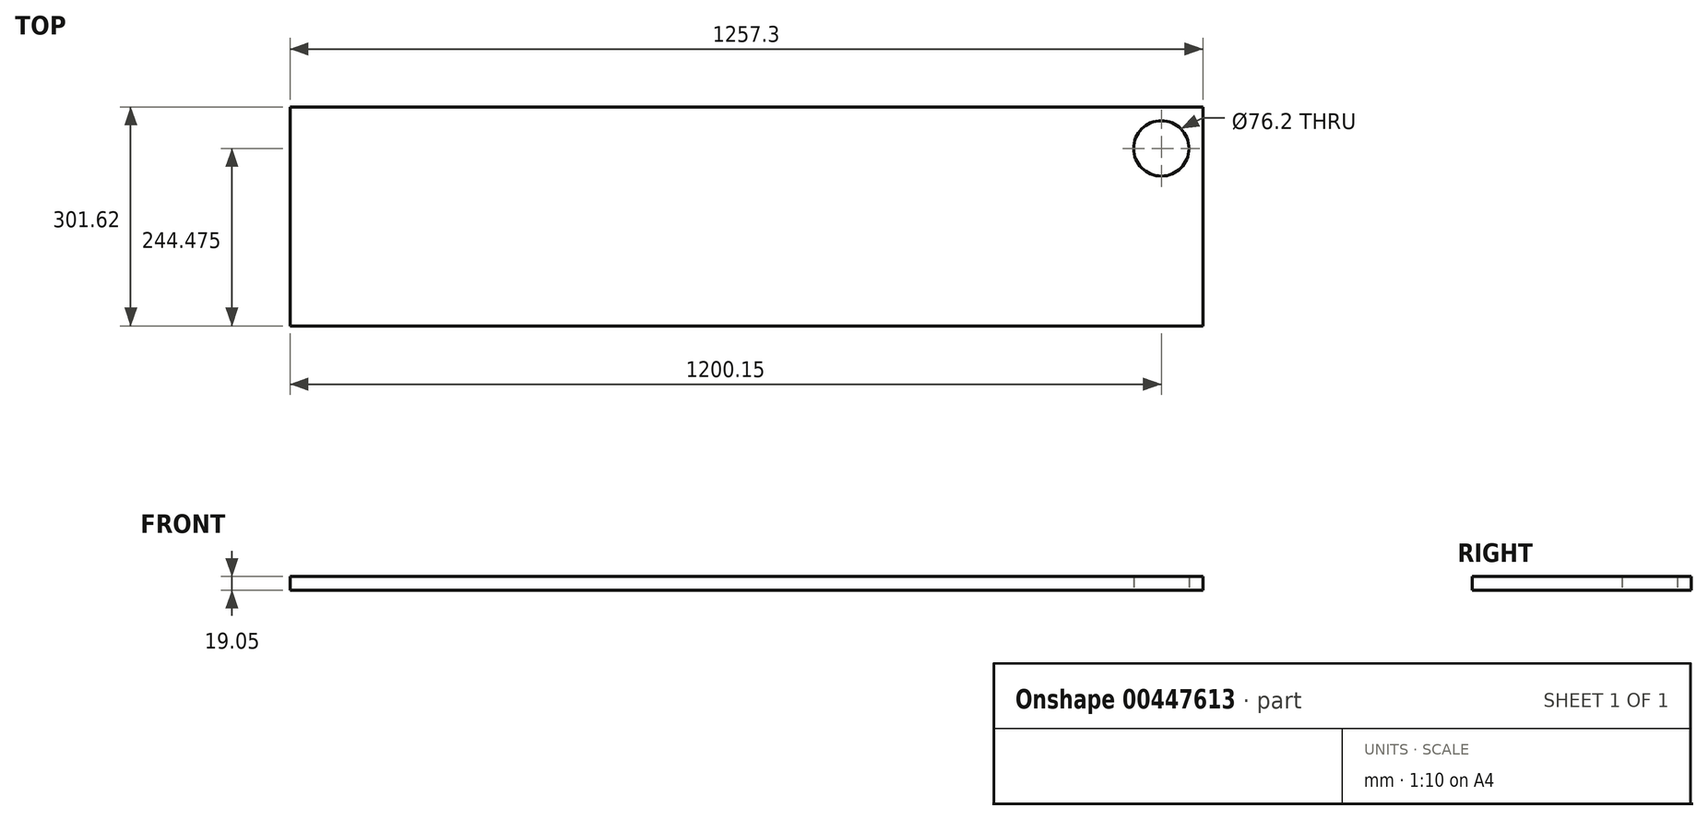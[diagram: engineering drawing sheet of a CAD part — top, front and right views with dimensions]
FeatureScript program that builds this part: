
annotation { "Feature Type Name" : "Feature", "Feature Type Description" : "" }
export const myFeature = defineFeature(function(context is Context, id is Id, definition is map)
    precondition{}
    {
        {
            var Q0;
            Q0=qCreatedBy(makeId("Top.planeOp"),FACE);
            var sketch = newSketch(context, id + "F0", { "sketchPlane" : qUnion([Q0])});
            skLineSegment(sketch, "E0.bottom", {"start": v(0, 0) * mm, "end": v(1257.3, 0) * mm});
            skLineSegment(sketch, "E0.top", {"start": v(0, 301.63) * mm, "end": v(1257.3, 301.63) * mm});
            skLineSegment(sketch, "E0.left", {"start": v(0, 0) * mm, "end": v(0, 301.63) * mm});
            skLineSegment(sketch, "E0.right", {"start": v(1257.3, 0) * mm, "end": v(1257.3, 301.63) * mm});
            skSolve(sketch);
        }
        {
            var Q0;
            Q0 = qSketchRegion(id + "F0", true);
            extrude(context, id + "F1", {"entities" : qUnion([Q0]), "depth" : 19.05 * mm});
        }
        {
            var Q0;
            Q0=makeQuery(id+"F1.opExtrude","CAP_FACE",FACE,{"disambiguationData":[OSD([sQuery(id+"F0.wireOp",EDGE,"E0.bottom"),sQuery(id+"F0.wireOp",EDGE,"E0.top"),sQuery(id+"F0.wireOp",EDGE,"E0.left"),sQuery(id+"F0.wireOp",EDGE,"E0.right")])],"isStart":true});
            var sketch = newSketch(context, id + "F2", { "sketchPlane" : qUnion([Q0])});
            skCircle(sketch, "E1", {"center": v(1200.15, -244.48) * mm, "radius": 38.1 * mm});
            skSolve(sketch);
        }
        {
            var Q0;
            Q0 = qSketchRegion(id + "F2", true);
            extrude(context, id + "F3", {"entities" : qUnion([Q0]), "operationType" : NewBodyOperationType.REMOVE, "endBound" : BoundingType.THROUGH_ALL, "oppositeDirection" : true, "depth" : 25.4 * mm, "offsetDistance" : 25.4 * mm});
        }
    });
